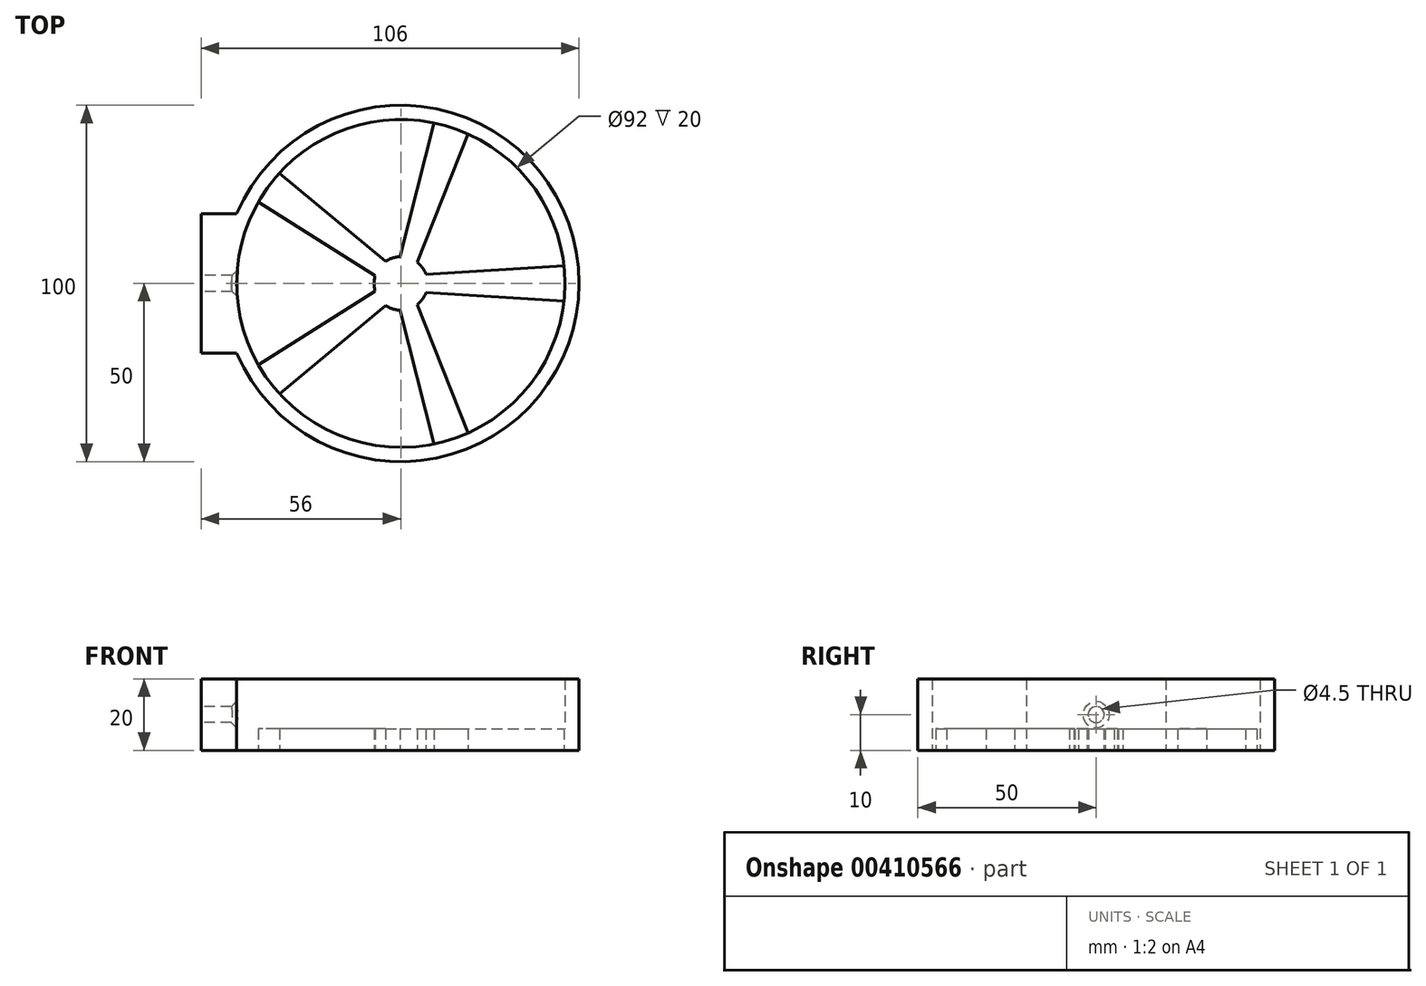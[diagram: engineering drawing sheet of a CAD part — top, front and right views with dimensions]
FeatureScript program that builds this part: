
annotation { "Feature Type Name" : "Feature", "Feature Type Description" : "" }
export const myFeature = defineFeature(function(context is Context, id is Id, definition is map)
    precondition{}
    {
        {
            var Q0;
            Q0=qCreatedBy(makeId("Top.planeOp"),FACE);
            var sketch = newSketch(context, id + "F0", { "sketchPlane" : qUnion([Q0])});
            skArc(sketch, "E0", {"start": v(-46, -19.6) * mm, "mid": v(50, 0) * mm, "end": v(-46, 19.6) * mm});
            skLineSegment(sketch, "E1", {"start": v(-46, -19.6) * mm, "end": v(-46, 19.6) * mm, "construction": true});
            skLineSegment(sketch, "E2", {"start": v(-46, 19.6) * mm, "end": v(-56, 19.6) * mm});
            skLineSegment(sketch, "E3", {"start": v(-46, -19.6) * mm, "end": v(-56, -19.6) * mm});
            skLineSegment(sketch, "E4", {"start": v(-56, -19.6) * mm, "end": v(-56, 19.6) * mm});
            skCircle(sketch, "E5", {"center": v(0, 0) * mm, "radius": 46 * mm});
            skSolve(sketch);
        }
        {
            var Q0;
            Q0 = qSketchRegion(id + "F0", true);
            extrude(context, id + "F1", {"entities" : qUnion([Q0]), "depth" : 20 * mm});
        }
        {
            var Q0;
            Q0=makeQuery(id+"F1.opExtrude","CAP_FACE",FACE,{"disambiguationData":[OSD([sQuery(id+"F0.wireOp",EDGE,"E0"),sQuery(id+"F0.wireOp",EDGE,"E2"),sQuery(id+"F0.wireOp",EDGE,"E3"),sQuery(id+"F0.wireOp",EDGE,"E4"),sQuery(id+"F0.wireOp",EDGE,"E5")])],"isStart":true});
            var sketch = newSketch(context, id + "F2", { "sketchPlane" : qUnion([Q0])});
            skPoint(sketch, "E6", {"position": v(0, 0) * mm});
            skCircle(sketch, "E7", {"center": v(0, 0) * mm, "radius": 7.5 * mm});
            skLineSegment(sketch, "E8", {"start": v(-0.2, 7.5) * mm, "end": v(9.38, 45.03) * mm});
            skLineSegment(sketch, "E9", {"start": v(4.56, 5.95) * mm, "end": v(18.89, 41.94) * mm});
            skLineSegment(sketch, "E10", {"start": v(9.38, 45.03) * mm, "end": v(18.89, 41.94) * mm, "construction": true});
            skLineSegment(sketch, "E11", {"start": v(-0.2, 7.5) * mm, "end": v(4.56, 5.95) * mm, "construction": true});
            skLineSegment(sketch, "E12.1.0", {"start": v(-7.2, 2.13) * mm, "end": v(-39.93, 22.83) * mm});
            skLineSegment(sketch, "E12.1.1", {"start": v(-4.25, 6.18) * mm, "end": v(-34.06, 30.92) * mm});
            skLineSegment(sketch, "E12.1.2", {"start": v(-39.93, 22.83) * mm, "end": v(-34.06, 30.92) * mm, "construction": true});
            skLineSegment(sketch, "E12.1.3", {"start": v(-7.2, 2.13) * mm, "end": v(-4.25, 6.18) * mm, "construction": true});
            skLineSegment(sketch, "E12.2.0", {"start": v(-4.25, -6.18) * mm, "end": v(-34.06, -30.92) * mm});
            skLineSegment(sketch, "E12.2.1", {"start": v(-7.2, -2.13) * mm, "end": v(-39.93, -22.83) * mm});
            skLineSegment(sketch, "E12.2.2", {"start": v(-34.06, -30.92) * mm, "end": v(-39.93, -22.83) * mm, "construction": true});
            skLineSegment(sketch, "E12.2.3", {"start": v(-4.25, -6.18) * mm, "end": v(-7.2, -2.13) * mm, "construction": true});
            skLineSegment(sketch, "E13.1.3.0", {"start": v(4.56, -5.95) * mm, "end": v(18.89, -41.94) * mm});
            skLineSegment(sketch, "E13.3.3.0", {"start": v(-0.2, -7.5) * mm, "end": v(9.38, -45.03) * mm});
            skLineSegment(sketch, "E13.6.3.0", {"start": v(18.89, -41.94) * mm, "end": v(9.38, -45.03) * mm, "construction": true});
            skLineSegment(sketch, "E13.9.3.0", {"start": v(4.56, -5.95) * mm, "end": v(-0.2, -7.5) * mm, "construction": true});
            skLineSegment(sketch, "E13.1.4.0", {"start": v(7.07, 2.5) * mm, "end": v(45.73, 5) * mm});
            skLineSegment(sketch, "E13.3.4.0", {"start": v(7.07, -2.5) * mm, "end": v(45.73, -5) * mm});
            skLineSegment(sketch, "E13.6.4.0", {"start": v(45.73, 5) * mm, "end": v(45.73, -5) * mm, "construction": true});
            skLineSegment(sketch, "E13.9.4.0", {"start": v(7.07, 2.5) * mm, "end": v(7.07, -2.5) * mm, "construction": true});
            skSolve(sketch);
        }
        {
            var Q0;
            Q0 = qSketchRegion(id + "F2", true);
            var Q1;
            {var subQ0=sQuery(id+"F2.wireOp",EDGE,"E12.1.0");Q1=makeQuery(id+"F2.imprint","IMPRINT",FACE,{"disambiguationData":[TD([[makeQuery(id+"F2.imprint","IMPRINT",EDGE,{"derivedFrom":subQ0}),-1.0]])]});}
            var Q2;
            {var subQ0=sQuery(id+"F2.wireOp",EDGE,"E8");Q2=makeQuery(id+"F2.imprint","IMPRINT",FACE,{"disambiguationData":[TD([[makeQuery(id+"F2.imprint","IMPRINT",EDGE,{"derivedFrom":subQ0}),-1.0]])]});}
            var Q3;
            {var subQ0=sQuery(id+"F2.wireOp",EDGE,"E13.1.4.0");Q3=makeQuery(id+"F2.imprint","IMPRINT",FACE,{"disambiguationData":[TD([[makeQuery(id+"F2.imprint","IMPRINT",EDGE,{"derivedFrom":subQ0}),-1.0]])]});}
            var Q4;
            {var subQ0=sQuery(id+"F2.wireOp",EDGE,"E13.1.3.0");Q4=makeQuery(id+"F2.imprint","IMPRINT",FACE,{"disambiguationData":[TD([[makeQuery(id+"F2.imprint","IMPRINT",EDGE,{"derivedFrom":subQ0}),-1.0]])]});}
            var Q5;
            {var subQ0=sQuery(id+"F2.wireOp",EDGE,"E12.2.0");Q5=makeQuery(id+"F2.imprint","IMPRINT",FACE,{"disambiguationData":[TD([[makeQuery(id+"F2.imprint","IMPRINT",EDGE,{"derivedFrom":subQ0}),-1.0]])]});}
            extrude(context, id + "F3", {"entities" : qUnion([Q0, Q1, Q2, Q3, Q4, Q5]), "operationType" : NewBodyOperationType.ADD, "oppositeDirection" : true, "depth" : 6 * mm});
        }
        {
            var Q0;
            Q0=makeQuery(id+"F1.opExtrude","SWEPT_FACE",FACE,{"disambiguationData":[OSD([sQuery(id+"F0.wireOp",EDGE,"E4")])]});
            var sketch = newSketch(context, id + "F4", { "sketchPlane" : qUnion([Q0])});
            skLineSegment(sketch, "E14", {"start": v(-19.6, 20) * mm, "end": v(19.6, 0) * mm, "construction": true});
            skCircle(sketch, "E15", {"center": v(0, 10) * mm, "radius": 2.25 * mm});
            skSolve(sketch);
        }
        {
            var Q0;
            Q0 = qSketchRegion(id + "F4", true);
            extrude(context, id + "F5", {"entities" : qUnion([Q0]), "operationType" : NewBodyOperationType.REMOVE, "oppositeDirection" : true, "depth" : 25 * mm});
        }
        {
            var Q0;
            Q0=makeQuery(id+"F5.boolean.opBoolean","INTERSECT",EDGE,{"derivedFrom":[makeQuery(id+"F1.opExtrude","SWEPT_FACE",FACE,{"disambiguationData":[OSD([sQuery(id+"F0.wireOp",EDGE,"E5")])]}),makeQuery(id+"F5.opExtrude","SWEPT_FACE",FACE,{"disambiguationData":[OSD([sQuery(id+"F4.wireOp",EDGE,"E15")])]})]});
            chamfer(context, id + "F6", {"entities" : qUnion([Q0]), "width" : 1.5 * mm, "tangentPropagation" : true});
        }
    });
